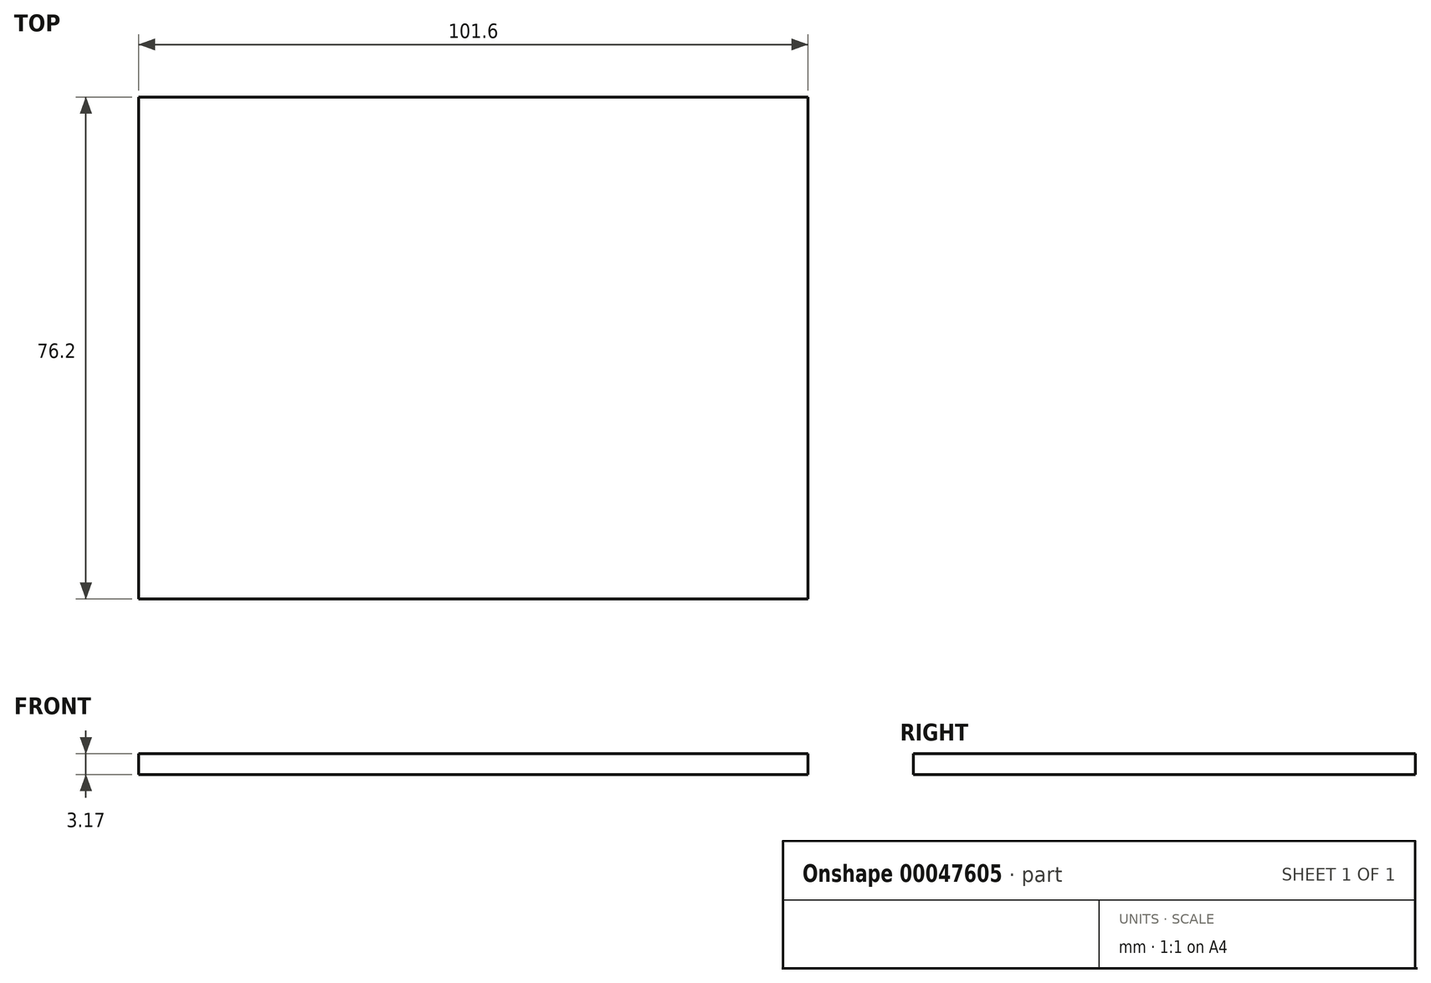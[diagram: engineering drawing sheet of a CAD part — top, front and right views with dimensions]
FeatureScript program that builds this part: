
annotation { "Feature Type Name" : "Feature", "Feature Type Description" : "" }
export const myFeature = defineFeature(function(context is Context, id is Id, definition is map)
    precondition{}
    {
        {
            var Q0;
            Q0=qCreatedBy(makeId("Top.planeOp"),FACE);
            var sketch = newSketch(context, id + "F0", { "sketchPlane" : qUnion([Q0])});
            skLineSegment(sketch, "E0.rect.bottom", {"start": v(50.8, -38.1) * mm, "end": v(-50.8, -38.1) * mm});
            skLineSegment(sketch, "E0.rect.top", {"start": v(50.8, 38.1) * mm, "end": v(-50.8, 38.1) * mm});
            skLineSegment(sketch, "E0.rect.left", {"start": v(50.8, -38.1) * mm, "end": v(50.8, 38.1) * mm});
            skLineSegment(sketch, "E0.rect.right", {"start": v(-50.8, -38.1) * mm, "end": v(-50.8, 38.1) * mm});
            skPoint(sketch, "E0.rect.middle", {"position": v(0, 0) * mm});
            skSolve(sketch);
        }
        {
            var Q0;
            Q0=makeQuery(id+"F0.imprint","IMPRINT",FACE,{"disambiguationData":[TD([[makeQuery(id+"F0.imprint","IMPRINT",EDGE,{"derivedFrom":sQuery(id+"F0.wireOp",EDGE,"E0.rect.bottom")}),-1.0]])]});
            extrude(context, id + "F1", {"entities" : qUnion([Q0]), "depth" : 3.17 * mm});
        }
    });
